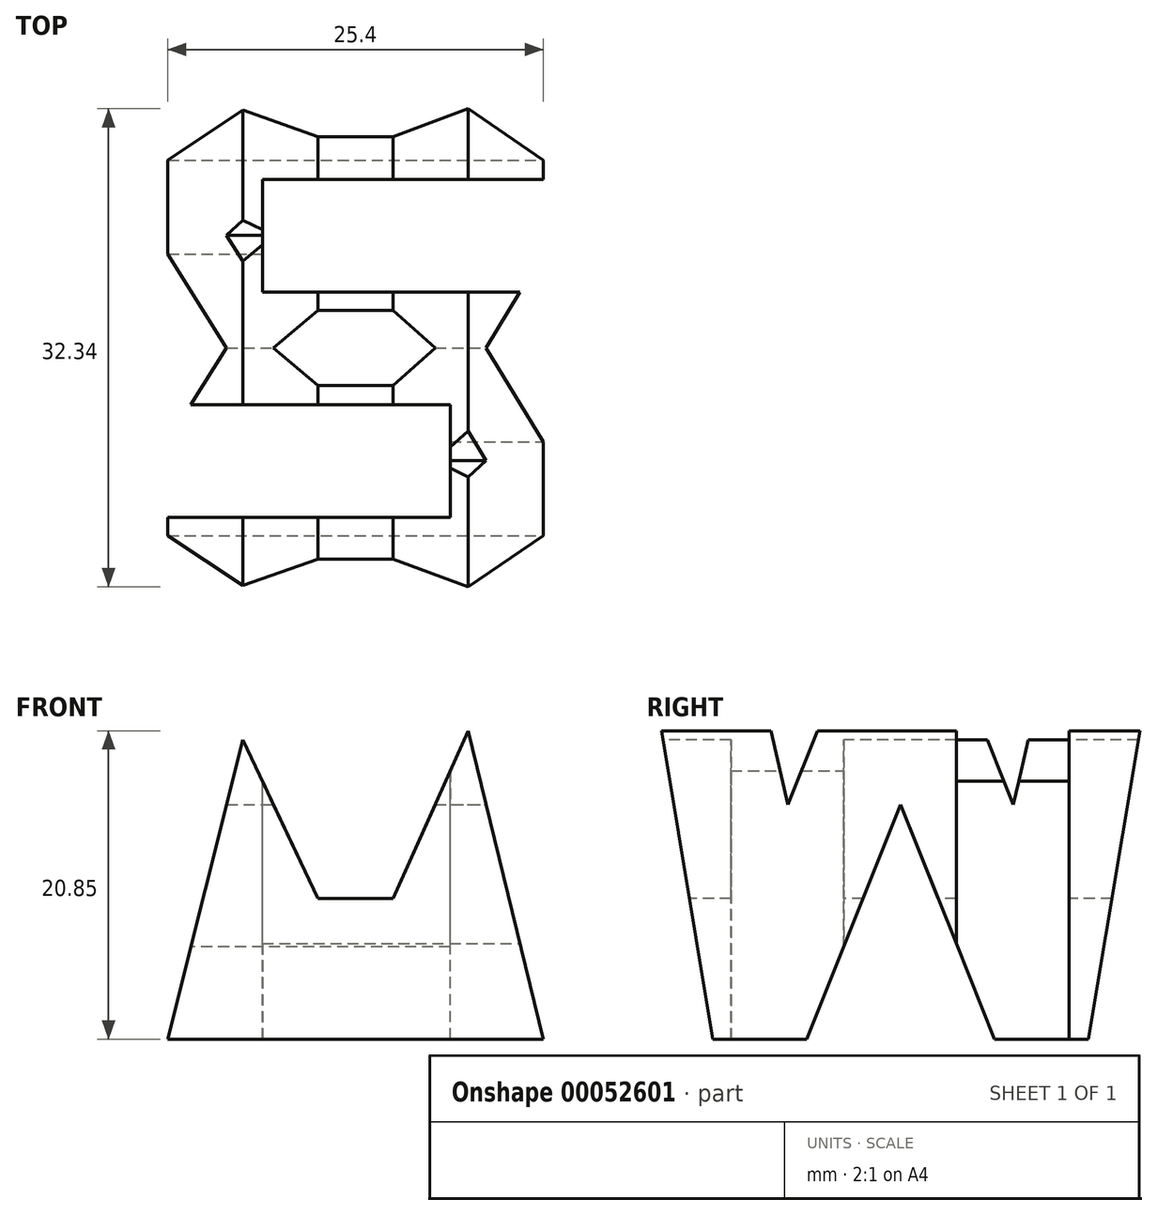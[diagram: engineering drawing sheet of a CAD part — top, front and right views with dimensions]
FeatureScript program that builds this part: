
annotation { "Feature Type Name" : "Feature", "Feature Type Description" : "" }
export const myFeature = defineFeature(function(context is Context, id is Id, definition is map)
    precondition{}
    {
        {
            var Q0;
            Q0=qCreatedBy(makeId("Front.planeOp"),FACE);
            var sketch = newSketch(context, id + "F0", { "sketchPlane" : qUnion([Q0])});
            skLineSegment(sketch, "E0", {"start": v(0, 0) * mm, "end": v(0, 38.1) * mm});
            skLineSegment(sketch, "E1", {"start": v(0, 38.1) * mm, "end": v(38.1, 38.1) * mm});
            skLineSegment(sketch, "E2", {"start": v(38.1, 38.1) * mm, "end": v(38.1, 0) * mm});
            skLineSegment(sketch, "E3", {"start": v(38.1, 0) * mm, "end": v(0, 0) * mm});
            skSolve(sketch);
        }
        {
            var Q0;
            Q0 = qSketchRegion(id + "F0", true);
            extrude(context, id + "F1", {"entities" : qUnion([Q0]), "depth" : 38.1 * mm});
        }
        {
            var Q0;
            Q0=qCreatedBy(makeId("Front.planeOp"),FACE);
            cPlane(context, id + "F2", {"entities" : qUnion([Q0]), "cplaneType" : CPlaneType.OFFSET, "offset" : 38.1 * mm, "width" : 152.4 * mm, "height" : 152.4 * mm});
        }
        {
            var Q0;
            Q0=qCreatedBy(makeId("Right.planeOp"),FACE);
            cPlane(context, id + "F3", {"entities" : qUnion([Q0]), "cplaneType" : CPlaneType.OFFSET, "offset" : 38.1 * mm, "width" : 152.4 * mm, "height" : 152.4 * mm});
        }
        {
            var Q0;
            Q0=qCreatedBy(makeId("Top.planeOp"),FACE);
            cPlane(context, id + "F4", {"entities" : qUnion([Q0]), "cplaneType" : CPlaneType.OFFSET, "offset" : 38.1 * mm, "width" : 152.4 * mm, "height" : 152.4 * mm});
        }
        {
            var Q0;
            Q0=qCreatedBy(id+"F3.planeOp",FACE);
            var sketch = newSketch(context, id + "F5", { "sketchPlane" : qUnion([Q0])});
            skLineSegment(sketch, "E4", {"start": v(-38.1, 38.1) * mm, "end": v(-31.75, 0) * mm});
            skLineSegment(sketch, "E5", {"start": v(-31.75, 0) * mm, "end": v(-25.4, 0) * mm});
            skLineSegment(sketch, "E6", {"start": v(-25.4, 0) * mm, "end": v(-19.05, 15.88) * mm});
            skLineSegment(sketch, "E7", {"start": v(-19.05, 15.88) * mm, "end": v(-12.7, 0) * mm});
            skLineSegment(sketch, "E8", {"start": v(-12.7, 0) * mm, "end": v(-6.35, 0) * mm});
            skLineSegment(sketch, "E9", {"start": v(-6.35, 0) * mm, "end": v(0, 38.1) * mm});
            skLineSegment(sketch, "E10", {"start": v(0, 38.1) * mm, "end": v(-6.35, 38.1) * mm});
            skLineSegment(sketch, "E11", {"start": v(-6.35, 38.1) * mm, "end": v(-11.43, 15.88) * mm});
            skLineSegment(sketch, "E12", {"start": v(-11.43, 15.88) * mm, "end": v(-16.51, 28.58) * mm});
            skLineSegment(sketch, "E13", {"start": v(-16.51, 28.58) * mm, "end": v(-21.59, 28.58) * mm});
            skLineSegment(sketch, "E14", {"start": v(-21.6, 28.58) * mm, "end": v(-26.67, 15.88) * mm});
            skLineSegment(sketch, "E15", {"start": v(-26.67, 15.88) * mm, "end": v(-31.75, 38.1) * mm});
            skLineSegment(sketch, "E16", {"start": v(-31.75, 38.1) * mm, "end": v(-38.1, 38.1) * mm});
            skLineSegment(sketch, "E17.bottom", {"start": v(0, 0) * mm, "end": v(-38.1, 0) * mm});
            skLineSegment(sketch, "E17.top", {"start": v(0, 38.1) * mm, "end": v(-38.1, 38.1) * mm});
            skLineSegment(sketch, "E17.left", {"start": v(0, 0) * mm, "end": v(0, 38.1) * mm});
            skLineSegment(sketch, "E17.right", {"start": v(-38.1, 0) * mm, "end": v(-38.1, 38.1) * mm});
            skSolve(sketch);
        }
        {
            var Q0;
            {var subQ1=sQuery(id+"F5.wireOp",EDGE,"E11");Q0=makeQuery(id+"F5.imprint","IMPRINT",FACE,{"disambiguationData":[TD([[makeQuery(id+"F5.imprint","IMPRINT",EDGE,{"derivedFrom":subQ1}),-1.0]])]});}
            var Q1;
            {var subQ0=sQuery(id+"F5.wireOp",EDGE,"E4");Q1=makeQuery(id+"F5.imprint","IMPRINT",FACE,{"disambiguationData":[TD([[makeQuery(id+"F5.imprint","IMPRINT",EDGE,{"derivedFrom":subQ0}),-1.0]])]});}
            var Q2;
            {var subQ0=sQuery(id+"F5.wireOp",EDGE,"E6");Q2=makeQuery(id+"F5.imprint","IMPRINT",FACE,{"disambiguationData":[TD([[makeQuery(id+"F5.imprint","IMPRINT",EDGE,{"derivedFrom":subQ0}),-1.0]])]});}
            var Q3;
            {var subQ0=sQuery(id+"F5.wireOp",EDGE,"E9");Q3=makeQuery(id+"F5.imprint","IMPRINT",FACE,{"disambiguationData":[TD([[makeQuery(id+"F5.imprint","IMPRINT",EDGE,{"derivedFrom":subQ0}),-1.0]])]});}
            extrude(context, id + "F6", {"entities" : qUnion([Q0, Q1, Q2, Q3]), "operationType" : NewBodyOperationType.REMOVE, "oppositeDirection" : true, "depth" : 38.1 * mm});
        }
        {
            var Q0;
            Q0=qCreatedBy(id+"F2.planeOp",FACE);
            var sketch = newSketch(context, id + "F7", { "sketchPlane" : qUnion([Q0])});
            skLineSegment(sketch, "E18.bottom", {"start": v(0, 38.1) * mm, "end": v(38.1, 38.1) * mm});
            skLineSegment(sketch, "E18.top", {"start": v(0, 0) * mm, "end": v(38.1, 0) * mm});
            skLineSegment(sketch, "E18.left", {"start": v(0, 38.1) * mm, "end": v(0, 0) * mm});
            skLineSegment(sketch, "E18.right", {"start": v(38.1, 38.1) * mm, "end": v(38.1, 0) * mm});
            skLineSegment(sketch, "E19", {"start": v(38.1, 0) * mm, "end": v(31.75, 38.1) * mm});
            skLineSegment(sketch, "E20", {"start": v(31.75, 38.1) * mm, "end": v(25.4, 38.1) * mm});
            skLineSegment(sketch, "E21", {"start": v(25.4, 38.1) * mm, "end": v(19.05, 22.23) * mm});
            skLineSegment(sketch, "E22", {"start": v(19.05, 22.23) * mm, "end": v(12.7, 38.1) * mm});
            skLineSegment(sketch, "E23", {"start": v(12.7, 38.1) * mm, "end": v(6.35, 38.1) * mm});
            skLineSegment(sketch, "E24", {"start": v(6.35, 38.1) * mm, "end": v(0, 0) * mm});
            skLineSegment(sketch, "E25", {"start": v(6.35, 0) * mm, "end": v(0, 0) * mm});
            skLineSegment(sketch, "E26", {"start": v(6.35, 0) * mm, "end": v(11.43, 20.26) * mm});
            skLineSegment(sketch, "E27", {"start": v(11.43, 20.26) * mm, "end": v(16.51, 9.53) * mm});
            skLineSegment(sketch, "E28", {"start": v(16.51, 9.53) * mm, "end": v(21.6, 9.53) * mm});
            skLineSegment(sketch, "E29", {"start": v(21.6, 9.53) * mm, "end": v(26.67, 20.85) * mm});
            skLineSegment(sketch, "E30", {"start": v(26.67, 20.85) * mm, "end": v(31.75, 0) * mm});
            skLineSegment(sketch, "E31", {"start": v(31.75, 0) * mm, "end": v(38.1, 0) * mm});
            skSolve(sketch);
        }
        {
            var Q0;
            {var subQ0=sQuery(id+"F7.wireOp",EDGE,"E21");Q0=makeQuery(id+"F7.imprint","IMPRINT",FACE,{"disambiguationData":[TD([[makeQuery(id+"F7.imprint","IMPRINT",EDGE,{"derivedFrom":subQ0}),-1.0]])]});}
            var Q1;
            {var subQ0=sQuery(id+"F7.wireOp",EDGE,"E18.right");Q1=makeQuery(id+"F7.imprint","IMPRINT",FACE,{"disambiguationData":[TD([[makeQuery(id+"F7.imprint","IMPRINT",EDGE,{"derivedFrom":subQ0}),-1.0]])]});}
            var Q2;
            Q2=makeQuery(id+"F7.imprint","IMPRINT",FACE,{"disambiguationData":[TD([[makeQuery(id+"F7.imprint","IMPRINT",EDGE,{"derivedFrom":sQuery(id+"F7.wireOp",EDGE,"E18.top")}),1.0]])]});
            var Q3;
            {var subQ0=sQuery(id+"F7.wireOp",EDGE,"E18.left");Q3=makeQuery(id+"F7.imprint","IMPRINT",FACE,{"disambiguationData":[TD([[makeQuery(id+"F7.imprint","IMPRINT",EDGE,{"derivedFrom":subQ0}),1.0]])]});}
            extrude(context, id + "F8", {"entities" : qUnion([Q0, Q1, Q2, Q3]), "operationType" : NewBodyOperationType.REMOVE, "oppositeDirection" : true, "depth" : 38.1 * mm});
        }
        {
            var Q0;
            Q0=qCreatedBy(id+"F4.planeOp",FACE);
            var sketch = newSketch(context, id + "F9", { "sketchPlane" : qUnion([Q0])});
            skLineSegment(sketch, "E32.bottom", {"start": v(0.05, -0.05) * mm, "end": v(38.15, -0.05) * mm});
            skLineSegment(sketch, "E32.top", {"start": v(0.05, -38.15) * mm, "end": v(38.15, -38.15) * mm});
            skLineSegment(sketch, "E32.left", {"start": v(0.05, -0.05) * mm, "end": v(0.05, -38.15) * mm});
            skLineSegment(sketch, "E32.right", {"start": v(38.15, -0.05) * mm, "end": v(38.15, -38.15) * mm});
            skLineSegment(sketch, "E33.bottom", {"start": v(38.15, -7.67) * mm, "end": v(12.75, -7.67) * mm});
            skLineSegment(sketch, "E33.top", {"start": v(38.15, -15.29) * mm, "end": v(12.75, -15.29) * mm});
            skLineSegment(sketch, "E33.left", {"start": v(38.15, -7.67) * mm, "end": v(38.15, -15.29) * mm});
            skLineSegment(sketch, "E33.right", {"start": v(12.75, -7.67) * mm, "end": v(12.75, -15.29) * mm});
            skLineSegment(sketch, "E34.bottom", {"start": v(0.05, -22.9) * mm, "end": v(25.45, -22.9) * mm});
            skLineSegment(sketch, "E34.top", {"start": v(0.05, -30.53) * mm, "end": v(25.45, -30.53) * mm});
            skLineSegment(sketch, "E34.left", {"start": v(0.05, -22.9) * mm, "end": v(0.05, -30.53) * mm});
            skLineSegment(sketch, "E34.right", {"start": v(25.45, -22.9) * mm, "end": v(25.45, -30.53) * mm});
            skSolve(sketch);
        }
        {
            var Q0;
            Q0=makeQuery(id+"F9.imprint","IMPRINT",FACE,{"disambiguationData":[TD([[makeQuery(id+"F9.imprint","IMPRINT",EDGE,{"derivedFrom":sQuery(id+"F9.wireOp",EDGE,"E33.bottom")}),1.0]])]});
            var Q1;
            Q1=makeQuery(id+"F9.imprint","IMPRINT",FACE,{"disambiguationData":[TD([[makeQuery(id+"F9.imprint","IMPRINT",EDGE,{"derivedFrom":sQuery(id+"F9.wireOp",EDGE,"E34.bottom")}),-1.0]])]});
            extrude(context, id + "F10", {"entities" : qUnion([Q0, Q1]), "operationType" : NewBodyOperationType.REMOVE, "oppositeDirection" : true, "depth" : 38.1 * mm});
        }
    });
